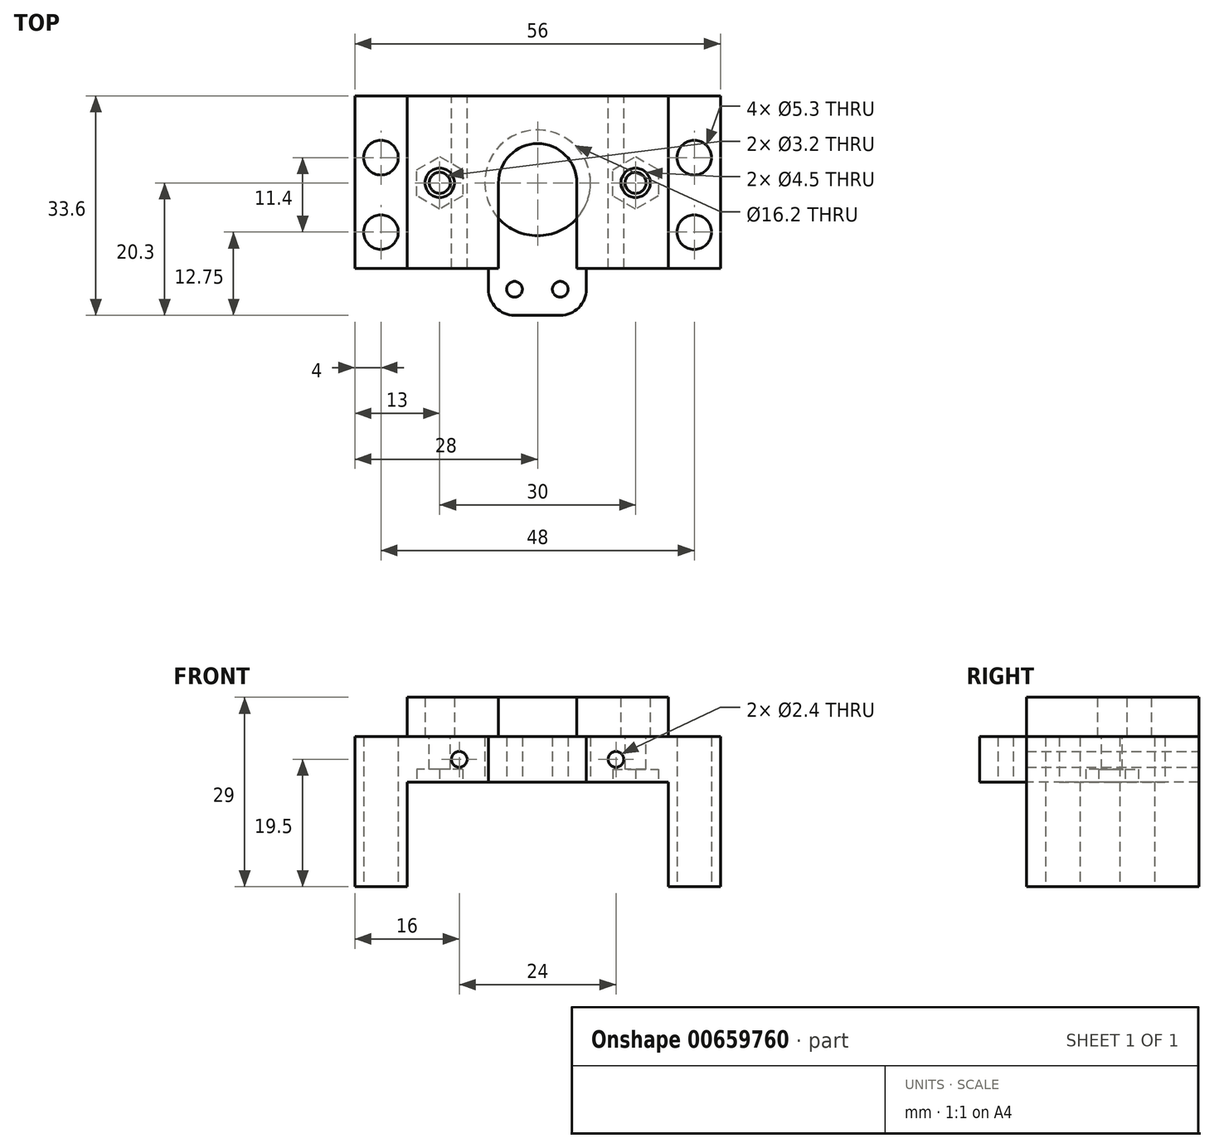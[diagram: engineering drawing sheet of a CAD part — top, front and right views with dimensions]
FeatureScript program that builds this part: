
annotation { "Feature Type Name" : "Feature", "Feature Type Description" : "" }
export const myFeature = defineFeature(function(context is Context, id is Id, definition is map)
    precondition{}
    {
        {
            var Q0;
            Q0=qCreatedBy(makeId("Top.planeOp"),FACE);
            var sketch = newSketch(context, id + "F0", { "sketchPlane" : qUnion([Q0])});
            skLineSegment(sketch, "E0.0", {"start": v(-28, 15.3) * mm, "end": v(-28, -11.1) * mm});
            skLineSegment(sketch, "E1.0", {"start": v(28, 15.3) * mm, "end": v(28, -11.1) * mm});
            skLineSegment(sketch, "E2.0", {"start": v(-20, 15.3) * mm, "end": v(-20, -11.1) * mm});
            skLineSegment(sketch, "E3.0", {"start": v(20, 15.3) * mm, "end": v(20, -11.1) * mm});
            skLineSegment(sketch, "E4.0", {"start": v(28, 15.3) * mm, "end": v(-28, 15.3) * mm});
            skLineSegment(sketch, "E5.0", {"start": v(7.46, -14.3) * mm, "end": v(7.46, -11.1) * mm});
            skArc(sketch, "E6.0", {"start": v(3.46, -18.3) * mm, "mid": v(6.29, -17.13) * mm, "end": v(7.46, -14.3) * mm});
            skLineSegment(sketch, "E7.0", {"start": v(3.46, -18.3) * mm, "end": v(-3.54, -18.3) * mm});
            skArc(sketch, "E8.0", {"start": v(-7.54, -14.3) * mm, "mid": v(-6.37, -17.13) * mm, "end": v(-3.54, -18.3) * mm});
            skLineSegment(sketch, "E9.0", {"start": v(-7.54, -14.3) * mm, "end": v(-7.54, -11.1) * mm});
            skCircle(sketch, "E10.0", {"center": v(-3.54, -14.3) * mm, "radius": 1.2 * mm});
            skCircle(sketch, "E11.0", {"center": v(3.46, -14.3) * mm, "radius": 1.2 * mm});
            skLineSegment(sketch, "E12.0", {"start": v(-28, -11.1) * mm, "end": v(-7.54, -11.1) * mm});
            skLineSegment(sketch, "E13.0", {"start": v(7.46, -11.1) * mm, "end": v(28, -11.1) * mm});
            skPoint(sketch, "E14.orphan", {"position": v(-11.5, 15.3) * mm});
            skPoint(sketch, "E15.orphan", {"position": v(11.5, 15.3) * mm});
            skPoint(sketch, "E16.orphan", {"position": v(28, 11.7) * mm});
            skPoint(sketch, "E17.orphan", {"position": v(20, 11.7) * mm});
            skPoint(sketch, "E18.orphan", {"position": v(-20, 11.7) * mm});
            skPoint(sketch, "E19.orphan", {"position": v(-28, 11.7) * mm});
            skCircle(sketch, "E20.0", {"center": v(-24, 5.85) * mm, "radius": 2 * mm, "construction": true});
            skCircle(sketch, "E21.0", {"center": v(-24, -5.55) * mm, "radius": 2 * mm, "construction": true});
            skCircle(sketch, "E22.0", {"center": v(24, 5.85) * mm, "radius": 2 * mm, "construction": true});
            skCircle(sketch, "E23.0", {"center": v(24, -5.55) * mm, "radius": 2 * mm, "construction": true});
            skCircle(sketch, "E24.0", {"center": v(0, 2) * mm, "radius": 8.1 * mm});
            skCircle(sketch, "E25", {"center": v(-24, 5.85) * mm, "radius": 2.65 * mm});
            skCircle(sketch, "E26", {"center": v(-24, -5.55) * mm, "radius": 2.65 * mm});
            skCircle(sketch, "E27", {"center": v(24, 5.85) * mm, "radius": 2.65 * mm});
            skCircle(sketch, "E28", {"center": v(24, -5.55) * mm, "radius": 2.65 * mm});
            skPoint(sketch, "E29.0", {"position": v(0, 0) * mm});
            skSolve(sketch);
        }
        {
            var Q0;
            {var subQ1=sQuery(id+"F0.wireOp",EDGE,"E2.0");Q0=makeQuery(id+"F0.imprint","IMPRINT",FACE,{"disambiguationData":[TD([[makeQuery(id+"F0.imprint","IMPRINT",EDGE,{"derivedFrom":subQ1}),1.0]])]});}
            var Q1;
            {var subQ1=sQuery(id+"F0.wireOp",EDGE,"E0.0");Q1=makeQuery(id+"F0.imprint","IMPRINT",FACE,{"disambiguationData":[TD([[makeQuery(id+"F0.imprint","IMPRINT",EDGE,{"derivedFrom":subQ1}),1.0]])]});}
            var Q2;
            {var subQ1=sQuery(id+"F0.wireOp",EDGE,"E1.0");Q2=makeQuery(id+"F0.imprint","IMPRINT",FACE,{"disambiguationData":[TD([[makeQuery(id+"F0.imprint","IMPRINT",EDGE,{"derivedFrom":subQ1}),-1.0]])]});}
            extrude(context, id + "F1", {"entities" : qUnion([Q0, Q1, Q2]), "depth" : 7 * mm, "offsetDistance" : 25 * mm});
        }
        {
            var Q0;
            {var subQ1=sQuery(id+"F0.wireOp",EDGE,"E1.0");Q0=makeQuery(id+"F0.imprint","IMPRINT",FACE,{"disambiguationData":[TD([[makeQuery(id+"F0.imprint","IMPRINT",EDGE,{"derivedFrom":subQ1}),-1.0]])]});}
            var Q1;
            {var subQ1=sQuery(id+"F0.wireOp",EDGE,"E0.0");Q1=makeQuery(id+"F0.imprint","IMPRINT",FACE,{"disambiguationData":[TD([[makeQuery(id+"F0.imprint","IMPRINT",EDGE,{"derivedFrom":subQ1}),1.0]])]});}
            extrude(context, id + "F2", {"entities" : qUnion([Q0, Q1]), "operationType" : NewBodyOperationType.ADD, "oppositeDirection" : true, "depth" : 16 * mm, "offsetDistance" : 25 * mm});
        }
        {
            var Q0;
            {var subQ0=sQuery(id+"F0.wireOp",EDGE,"E4.0");Q0=makeQuery(id+"F2.boolean.opBoolean","MERGE",FACE,{"derivedFrom":[makeQuery(id+"F1.opExtrude","SWEPT_FACE",FACE,{"disambiguationData":[OSD([subQ0])]}),makeQuery(id+"F2.opExtrude","SWEPT_FACE",FACE,{"disambiguationData":[OSD([subQ0]),TDD([makeQuery(id+"F0.imprint","IMPRINT",EDGE,{"disambiguationData":[TD([[makeQuery(id+"F0.imprint","INTERSECT",VERTEX,{"derivedFrom":[sQuery(id+"F0.wireOp",EDGE,"E1.0"),subQ0]}),-1.0]])],"derivedFrom":subQ0})])]}),makeQuery(id+"F2.opExtrude","SWEPT_FACE",FACE,{"disambiguationData":[OSD([subQ0]),TDD([makeQuery(id+"F0.imprint","IMPRINT",EDGE,{"disambiguationData":[TD([[makeQuery(id+"F0.imprint","INTERSECT",VERTEX,{"derivedFrom":[sQuery(id+"F0.wireOp",EDGE,"E0.0"),subQ0]}),1.0]])],"derivedFrom":subQ0})])]})]});}
            var sketch = newSketch(context, id + "F3", { "sketchPlane" : qUnion([Q0])});
            skCircle(sketch, "E30.0", {"center": v(-12, 3.5) * mm, "radius": 1.6 * mm, "construction": true});
            skCircle(sketch, "E31.0", {"center": v(12, 3.5) * mm, "radius": 1.6 * mm, "construction": true});
            skPoint(sketch, "E32.0", {"position": v(-20, 0) * mm});
            skSolve(sketch);
        }
        {
            var Q0;
            Q0=sQuery(id+"F3.wireOp",VERTEX,"E30.0.center");
            var Q1;
            Q1=sQuery(id+"F3.wireOp",VERTEX,"E31.0.center");
            var Q2;
            Q2=makeQuery(id+"F1.opExtrude","SWEPT_BODY",BODY,{"disambiguationData":[OSD([sQuery(id+"F0.wireOp",EDGE,"E0.0"),sQuery(id+"F0.wireOp",EDGE,"E1.0"),sQuery(id+"F0.wireOp",EDGE,"E4.0"),sQuery(id+"F0.wireOp",EDGE,"E5.0"),sQuery(id+"F0.wireOp",EDGE,"E6.0"),sQuery(id+"F0.wireOp",EDGE,"E7.0"),sQuery(id+"F0.wireOp",EDGE,"E8.0"),sQuery(id+"F0.wireOp",EDGE,"E9.0"),sQuery(id+"F0.wireOp",EDGE,"E10.0"),sQuery(id+"F0.wireOp",EDGE,"E11.0"),sQuery(id+"F0.wireOp",EDGE,"E12.0"),sQuery(id+"F0.wireOp",EDGE,"E13.0"),sQuery(id+"F0.wireOp",EDGE,"E24.0"),sQuery(id+"F0.wireOp",EDGE,"E25"),sQuery(id+"F0.wireOp",EDGE,"E26"),sQuery(id+"F0.wireOp",EDGE,"E27"),sQuery(id+"F0.wireOp",EDGE,"E28")])]});
            hole(context, id + "F4", {"style" : HoleStyle.SIMPLE, "endStyle" : HoleEndStyle.THROUGH, "holeDiameter" : 2.4 * mm, "majorDiameter" : 5 * mm, "isTappedThrough" : true, "tappedDepth" : 12 * mm, "tapClearance" : 3, "locations" : qUnion([Q0, Q1]), "scope" : qUnion([Q2])});
        }
        {
            var Q0;
            Q0=makeQuery(id+"F1.opExtrude","CAP_FACE",FACE,{"disambiguationData":[OSD([sQuery(id+"F0.wireOp",EDGE,"E0.0"),sQuery(id+"F0.wireOp",EDGE,"E1.0"),sQuery(id+"F0.wireOp",EDGE,"E4.0"),sQuery(id+"F0.wireOp",EDGE,"E5.0"),sQuery(id+"F0.wireOp",EDGE,"E6.0"),sQuery(id+"F0.wireOp",EDGE,"E7.0"),sQuery(id+"F0.wireOp",EDGE,"E8.0"),sQuery(id+"F0.wireOp",EDGE,"E9.0"),sQuery(id+"F0.wireOp",EDGE,"E10.0"),sQuery(id+"F0.wireOp",EDGE,"E11.0"),sQuery(id+"F0.wireOp",EDGE,"E12.0"),sQuery(id+"F0.wireOp",EDGE,"E13.0"),sQuery(id+"F0.wireOp",EDGE,"E24.0"),sQuery(id+"F0.wireOp",EDGE,"E25"),sQuery(id+"F0.wireOp",EDGE,"E26"),sQuery(id+"F0.wireOp",EDGE,"E27"),sQuery(id+"F0.wireOp",EDGE,"E28")])],"isStart":false});
            var sketch = newSketch(context, id + "F5", { "sketchPlane" : qUnion([Q0])});
            skArc(sketch, "E33.0", {"start": v(6, 2) * mm, "mid": v(0, 8) * mm, "end": v(-6, 2) * mm});
            skLineSegment(sketch, "E34.0", {"start": v(-20, 15.3) * mm, "end": v(28, 15.3) * mm});
            skLineSegment(sketch, "E35.0", {"start": v(-6, -11.1) * mm, "end": v(-20, -11.1) * mm});
            skLineSegment(sketch, "E36", {"start": v(-6, 2) * mm, "end": v(-6, -11.1) * mm});
            skPoint(sketch, "E37.orphan", {"position": v(-7.54, -11.1) * mm});
            skLineSegment(sketch, "E38.0", {"start": v(-20, 15.3) * mm, "end": v(-20, -11.1) * mm});
            skPoint(sketch, "E39.orphan", {"position": v(-28, -11.1) * mm});
            skPoint(sketch, "E40.orphan", {"position": v(-28, 15.3) * mm});
            skLineSegment(sketch, "E41.MirrorCS", {"start": v(6, 2) * mm, "end": v(6, -11.1) * mm});
            skLineSegment(sketch, "E42.MirrorCS", {"start": v(6, -11.1) * mm, "end": v(20, -11.1) * mm});
            skLineSegment(sketch, "E43.MirrorCS", {"start": v(20, 15.3) * mm, "end": v(20, -11.1) * mm});
            skCircle(sketch, "E44.0", {"center": v(0, 2) * mm, "radius": 1.1 * mm, "construction": true});
            skLineSegment(sketch, "E45", {"start": v(20, 2) * mm, "end": v(8.1, 2) * mm, "construction": true});
            skCircle(sketch, "E46.0", {"center": v(0, 2) * mm, "radius": 8.1 * mm, "construction": true});
            skLineSegment(sketch, "E47.trimOffspring", {"start": v(-8.1, 2) * mm, "end": v(-20, 2) * mm, "construction": true});
            skLineSegment(sketch, "E48.trimOffspring", {"start": v(6, 2) * mm, "end": v(-6, 2) * mm, "construction": true});
            skPoint(sketch, "E49", {"position": v(-15, 2) * mm});
            skPoint(sketch, "E50", {"position": v(15, 2) * mm});
            skCircle(sketch, "E51", {"center": v(-15, 2) * mm, "radius": 1.6 * mm});
            skCircle(sketch, "E52", {"center": v(15, 2) * mm, "radius": 1.6 * mm});
            skCircle(sketch, "E53", {"center": v(-15, 2) * mm, "radius": 2.25 * mm});
            skCircle(sketch, "E54", {"center": v(15, 2) * mm, "radius": 2.25 * mm});
            skSolve(sketch);
        }
        {
            var Q0;
            Q0=makeQuery(id+"F5.imprint","IMPRINT",FACE,{"disambiguationData":[TD([[makeQuery(id+"F5.imprint","IMPRINT",EDGE,{"derivedFrom":sQuery(id+"F5.wireOp",EDGE,"E52")}),1.0]])]});
            var Q1;
            Q1=makeQuery(id+"F5.imprint","IMPRINT",FACE,{"disambiguationData":[TD([[makeQuery(id+"F5.imprint","IMPRINT",EDGE,{"derivedFrom":sQuery(id+"F5.wireOp",EDGE,"E51")}),1.0]])]});
            extrude(context, id + "F6", {"entities" : qUnion([Q0, Q1]), "operationType" : NewBodyOperationType.REMOVE, "oppositeDirection" : true, "depth" : 25 * mm, "offsetDistance" : 25 * mm});
        }
        {
            var Q0;
            {var subQ1=sQuery(id+"F0.wireOp",EDGE,"E2.0");Q0=makeQuery(id+"F0.imprint","IMPRINT",FACE,{"disambiguationData":[TD([[makeQuery(id+"F0.imprint","IMPRINT",EDGE,{"derivedFrom":subQ1}),1.0]])]});}
            var sketch = newSketch(context, id + "F7", { "sketchPlane" : qUnion([Q0])});
            skCircle(sketch, "E55.0", {"center": v(15, 2) * mm, "radius": 1.6 * mm, "construction": true});
            skCircle(sketch, "E55.1", {"center": v(-15, 2) * mm, "radius": 1.6 * mm, "construction": true});
            skCircle(sketch, "E56.cCircle", {"center": v(15, 2) * mm, "radius": 3.5 * mm, "construction": true});
            skLineSegment(sketch, "E56.0", {"start": v(11.5, -0.02) * mm, "end": v(11.5, 4.02) * mm});
            skLineSegment(sketch, "E56.1", {"start": v(11.5, 4.02) * mm, "end": v(15, 6.04) * mm});
            skLineSegment(sketch, "E56.2", {"start": v(15, 6.04) * mm, "end": v(18.5, 4.02) * mm});
            skLineSegment(sketch, "E56.3", {"start": v(18.5, 4.02) * mm, "end": v(18.5, -0.02) * mm});
            skLineSegment(sketch, "E56.4", {"start": v(18.5, -0.02) * mm, "end": v(15, -2.04) * mm});
            skLineSegment(sketch, "E56.5", {"start": v(15, -2.04) * mm, "end": v(11.5, -0.02) * mm});
            skPoint(sketch, "E56.0.midPoint", {"position": v(11.5, 2) * mm});
            skCircle(sketch, "E57.cCircle", {"center": v(-15, 2) * mm, "radius": 3.5 * mm, "construction": true});
            skLineSegment(sketch, "E57.0", {"start": v(-11.5, 4.02) * mm, "end": v(-11.5, -0.02) * mm});
            skLineSegment(sketch, "E57.1", {"start": v(-11.5, -0.02) * mm, "end": v(-15, -2.04) * mm});
            skLineSegment(sketch, "E57.2", {"start": v(-15, -2.04) * mm, "end": v(-18.5, -0.02) * mm});
            skLineSegment(sketch, "E57.3", {"start": v(-18.5, -0.02) * mm, "end": v(-18.5, 4.02) * mm});
            skLineSegment(sketch, "E57.4", {"start": v(-18.5, 4.02) * mm, "end": v(-15, 6.04) * mm});
            skLineSegment(sketch, "E57.5", {"start": v(-15, 6.04) * mm, "end": v(-11.5, 4.02) * mm});
            skPoint(sketch, "E57.0.midPoint", {"position": v(-11.5, 2) * mm});
            skPoint(sketch, "E58.0", {"position": v(0, 0) * mm});
            skSolve(sketch);
        }
        {
            var Q0;
            Q0=makeQuery(id+"F7.imprint","IMPRINT",FACE,{"disambiguationData":[TD([[makeQuery(id+"F7.imprint","IMPRINT",EDGE,{"derivedFrom":sQuery(id+"F7.wireOp",EDGE,"E57.0")}),-1.0]])]});
            var Q1;
            Q1=makeQuery(id+"F7.imprint","IMPRINT",FACE,{"disambiguationData":[TD([[makeQuery(id+"F7.imprint","IMPRINT",EDGE,{"derivedFrom":sQuery(id+"F7.wireOp",EDGE,"E56.0")}),-1.0]])]});
            extrude(context, id + "F8", {"entities" : qUnion([Q0, Q1]), "operationType" : NewBodyOperationType.REMOVE, "depth" : 2 * mm, "offsetDistance" : 25 * mm});
        }
        {
            var Q0;
            {var subQ9=sQuery(id+"F5.wireOp",EDGE,"E38.0");Q0=makeQuery(id+"F5.imprint","IMPRINT",FACE,{"disambiguationData":[TD([[makeQuery(id+"F5.imprint","IMPRINT",EDGE,{"derivedFrom":subQ9}),1.0]])]});}
            var Q1;
            {var subQ0=sQuery(id+"F5.wireOp",EDGE,"E33.0");Q1=makeQuery(id+"F5.imprint","IMPRINT",FACE,{"disambiguationData":[TD([[makeQuery(id+"F5.imprint","IMPRINT",EDGE,{"derivedFrom":subQ0}),-1.0]])]});}
            extrude(context, id + "F9", {"entities" : qUnion([Q0, Q1]), "depth" : 6 * mm, "offsetDistance" : 25 * mm});
        }
    });
